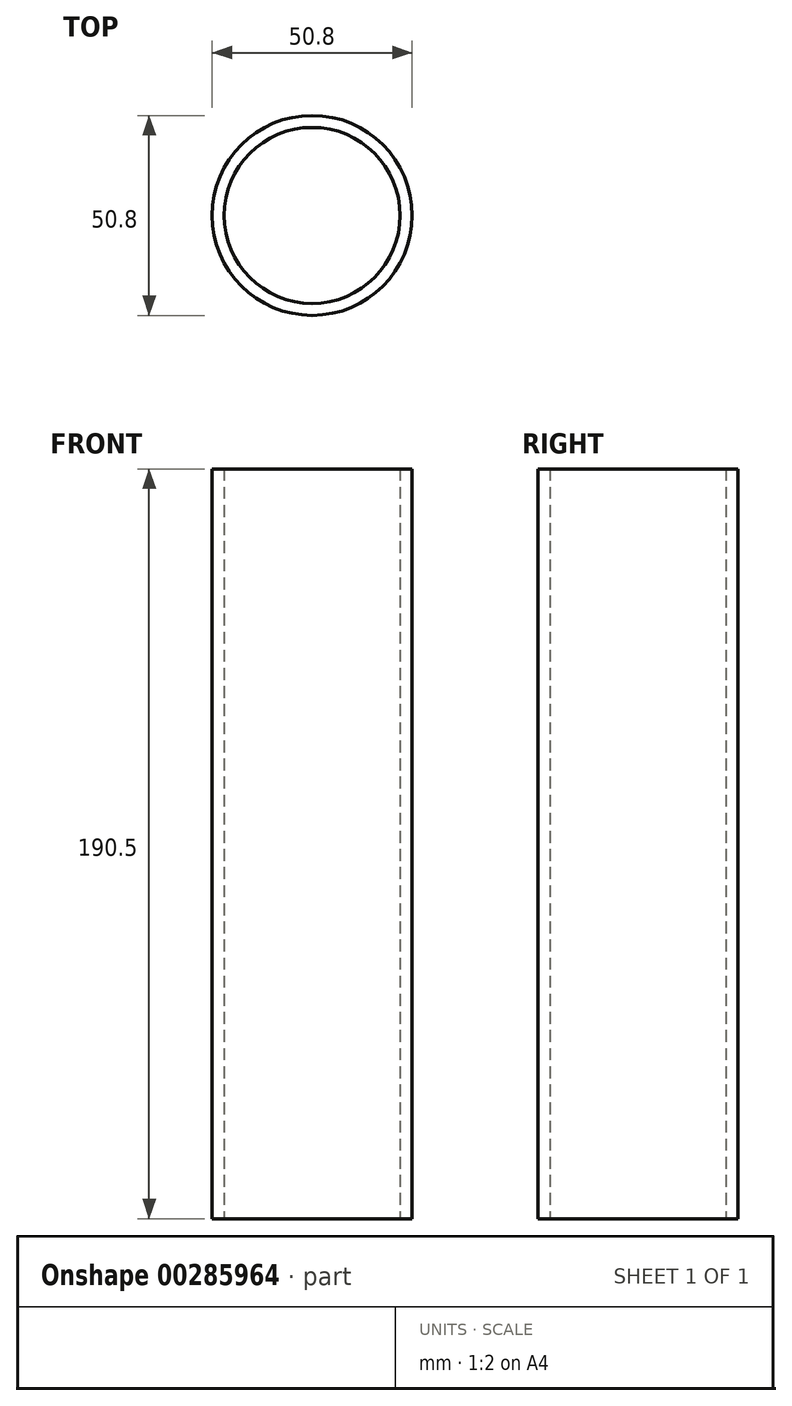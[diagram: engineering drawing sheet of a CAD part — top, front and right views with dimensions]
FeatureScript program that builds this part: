
annotation { "Feature Type Name" : "Feature", "Feature Type Description" : "" }
export const myFeature = defineFeature(function(context is Context, id is Id, definition is map)
    precondition{}
    {
        {
            var Q0;
            Q0=qCreatedBy(makeId("Top.planeOp"),FACE);
            var sketch = newSketch(context, id + "F0", { "sketchPlane" : qUnion([Q0])});
            skCircle(sketch, "E0", {"center": v(0, 0) * mm, "radius": 25.4 * mm});
            skCircle(sketch, "E1", {"center": v(0, 0) * mm, "radius": 22.35 * mm});
            skSolve(sketch);
        }
        {
            var Q0;
            Q0=makeQuery(id+"F0.imprint","IMPRINT",FACE,{"disambiguationData":[TD([[makeQuery(id+"F0.imprint","IMPRINT",EDGE,{"derivedFrom":sQuery(id+"F0.wireOp",EDGE,"E0")}),1.0]])]});
            extrude(context, id + "F1", {"entities" : qUnion([Q0]), "depth" : 190.5 * mm});
        }
    });
